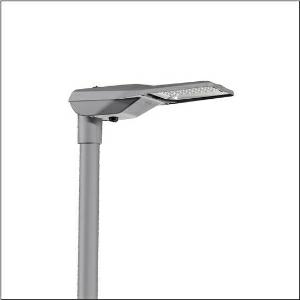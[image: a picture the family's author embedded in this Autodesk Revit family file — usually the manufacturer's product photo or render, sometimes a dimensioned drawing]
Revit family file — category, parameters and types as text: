
# Revit family: streetlight_sl_21_mini___st1_0a_5xe2d23t08hb_892b
name_source: partatom
category: Lighting Fixtures
units: mm (PartAtom-declared; Revit-internal decimal feet)

## family parameters
Cut with Voids When Loaded = No
Host = Face
Light Source = No
Part Type = Normal
Room Calculation Point = No
Round Connector Dimension = Use Diameter
Shared = No

## types (1)
- --- (1 x LED, 7490 lm, 66 W, 2200K)
    Apparent Load = 66 VA
    CIE Flux Codes = 37 72 97 100 100
    Color Rendering = 70
    Color Temperature = 2200K
    Default Elevation = 1800 mm
    Description = Streetlight SL 21 mini, mast luminaire, primary light control with lens, of PMMA, primary optical cover: cover, of toughened safety glass, transparent, light distribution: ST1.0a, light emission: direct distribution, primary light characteristic: asymmetric, installation type: side-entry, post-top, LED, High Power LED, rated luminous flux: 7.490lm, luminous efficacy: 114lm/W, light colour: 722, colour temperature: 2200K, control gear: D4i, control: overheat protection, constant luminous flux control, time-dependent luminous flux control, flexible luminous flux parameterisation, pre-setting: logarithmic dimming characteristic, mains connection: 220..240V, AC, 50/60Hz, start of lifetime: 66W, end of service life: 69W, reduction: 30W, luminaire housing, of diecast aluminium, powder-coated, Siteco® metallic grey (DB 702S), corrosivity category C5 mid according to DIN EN ISO 12944, please order mast flange separately, inclination adjustable: 0°, 5°, 10°, 15°, sealing non-destructively replaceable, multi-level sealing system, length: 628mm, width: 235mm, height: 110mm, mast flange for spigot size: 42mm (side-entry): 5XC10008XM4, 60/48mm (side-entry/post-top): 5XC10108XM2, 76/60mm (side-entry/post-top): 5XC10108XM1, mounting height: 4..8m, Smart Interface below and above, protection rating (complete): IP66, insulation class (complete): insulation class II (safety insulation), certification: CE, ENEC, ENEC+, VDE, impact resistance: IK10, permissible operating ambient temperature for outdoor applications: -40..+50°C, standard-compliant lighting for roads and squares, packaging unit: 1 piece

Light Distribution: ST1.0a
    Height = 110 mm
    Lamp = 1 x LED
    Lamp Light Flux = 7490 lm
    Lamp Power = 66 W
    Lamp count = 1
    Length = 625 mm
    Luminous efficacy = 113 lm/W
    Manufacturer = Siteco
    ModVariant = No
    Model = 5XE2D23T08HB
    Number of Poles = 1
    OnlyDefault = Yes
    Power Factor = 1
    Product Name = Streetlight SL 21 mini | ST1.0a
    Product group = mast luminaire | pylon top
    ProductGroupID = 6100
    Protection Class = Protection class II
    Protection Degree = IP 66
    RLX_Detail_Level = 1
    RLX_Emergency_Light_Flux = 0 lm
    RLX_Emergency_Type = 0
    RLX_Emergency_Type_DB = No
    RlxData = <blob elided: 26329 chars, md5=c9a11a97>
    Socket = socket
    Standby Power = 0 W
    System Light Flux = 7490 lm
    System Power = 66 W
    Type Comments = factory setting: luminous flux: 100 % | dim-lin: 254 | 670 mA
    Type Image = l_1003514.jpg
    URL = http://relux.com
    VarID = @adj_209807
    Voltage = 0 V
    Weight = 0.00 kg
    Width = 234 mm

## geometry (parser evidence)
native form markers: Blend x4, Sweep x12
no freeform markers — native parametric forms only
